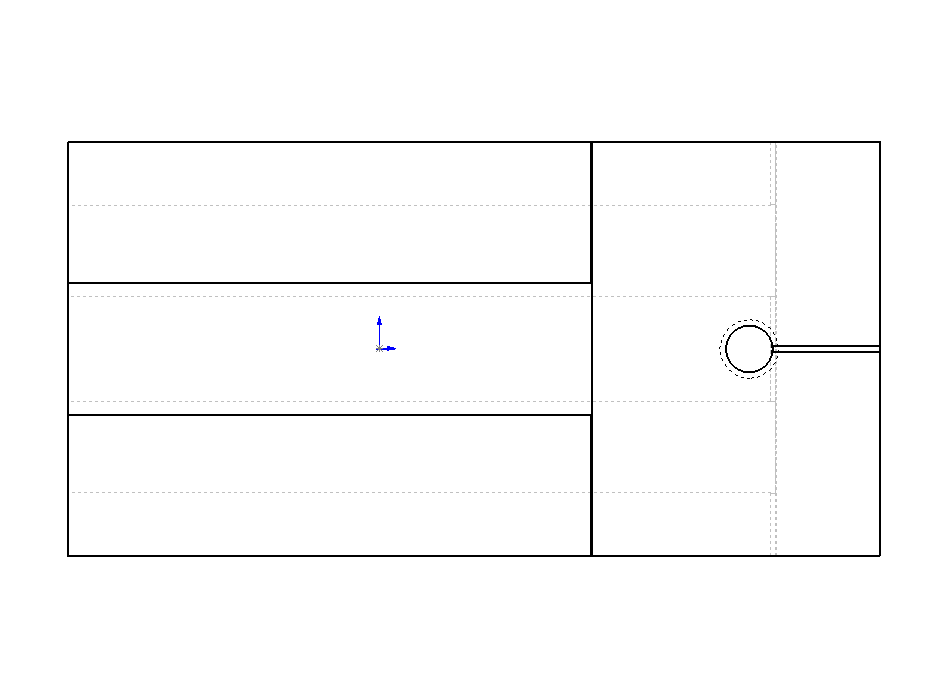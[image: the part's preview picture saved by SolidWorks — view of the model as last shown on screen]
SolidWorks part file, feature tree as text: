
SOLIDWORKS PART (.sldprt)
format: sldprt  version: not decoded by parser v0  size: 601,600 bytes
history: native  units: mm
features: sketch x11, cut_extrude x4, extrude x3, hole x2, material x1, thread x1, fillet x1 + 1 further entry (+11 scaffold rows collapsed)
feature tree (35):
  scaffold x11  (default folders/planes/origin — collapsed)
  material  "Material <not specified>"
  "Origin"  ID=-1
  sketch  "Sketch1"  dims[c1.D1=78.0mm c1.D2=12.0mm c1.D3=20.0mm c1.D4=40.0mm c2.D1=24.25mm]
  extrude  "Extrude1"  Depth=54.7mm
  sketch  "Sketch4"  dims[c1.D1=6.35mm c1.D4=6.35mm c1.D2=10.3mm c1.D3=12.7mm c2.D4=~5.199311mm]
  cut_extrude  "Cut-Extrude1"  [1 undecoded]
  sketch  "Sketch5"
  extrude  "Extrude2"  Depth=15.1mm
  hole  "#8 Clearance Hole1"  Diameter=4.4958mm Depth=39.35mm
  sketch  "Sketch7"  dims[D1=6.35mm D2=9.525mm]
  sketch  "Sketch6"  dims[hole-wizard template sketch: 60 standard entries collapsed; hole parameters kept: c18.Thru Hole Depth=39.35mm]
  hole  "#4-40 Tapped Hole1"  [1 undecoded]
  sketch  "Sketch10"  dims[D1=6.35mm]
  thread  "Cosmetic Thread1"  Diameter=5.6896mm  [1 undecoded]
  sketch  "Sketch9"  dims[hole-wizard template sketch: 47 standard entries collapsed; hole parameters kept: c15.Tap Drill Depth=8.8646mm c15.D3=~14.816244mm c15.Drill Angle=118.0deg]
  sketch  "Sketch11"  dims[D1=12.7mm]
  cut_extrude  "Cut-Extrude2"  Depth=5.08mm
  fillet  "Fillet1"  Radius=1.27mm
  sketch  "Sketch12"  dims[D1=0.25mm]
  cut_extrude  "Cut-Extrude3"  Depth=0.25mm
  sketch  "Sketch13"
  extrude  "Extrude3"  Depth=6.35mm
  sketch  "Sketch14"  dims[D1=0.25mm]
  cut_extrude  "Cut-Extrude4"  Depth=0.25mm
decode coverage: 18 of 22 modeling features carry decoded parameters; 1 rows unclassified (native names shown)
note: ~ marks probable driven/reference dimensions
note: 3 parameter values undecoded
note: suppression state not decoded; provenance and decode notes live in map.json
